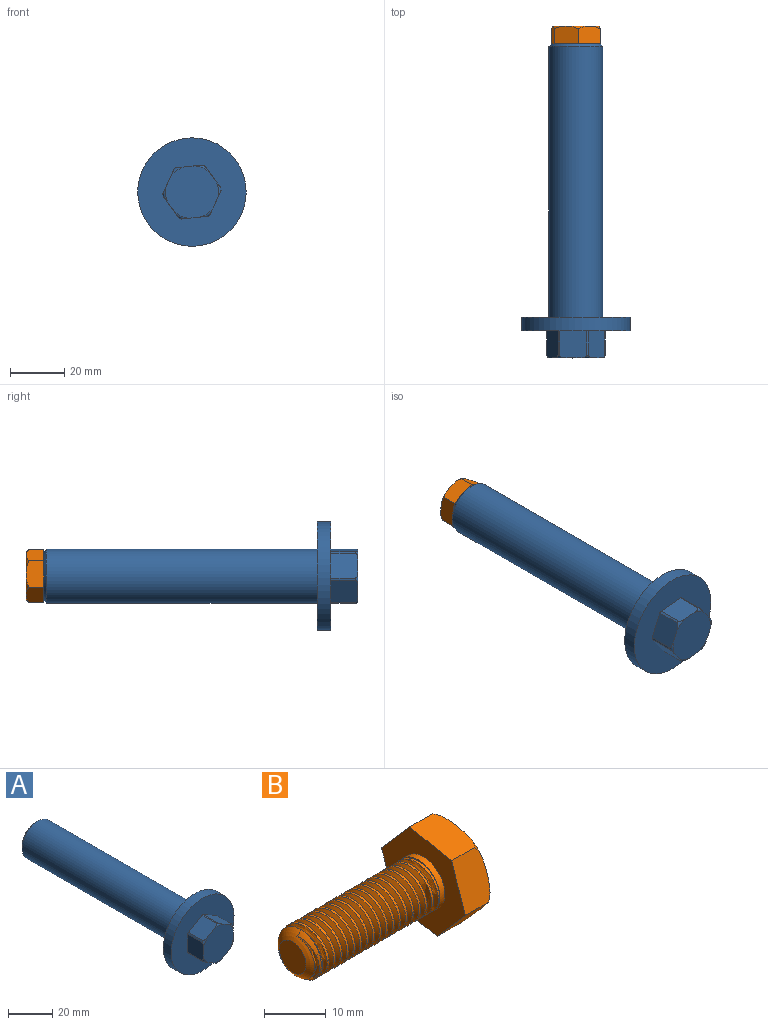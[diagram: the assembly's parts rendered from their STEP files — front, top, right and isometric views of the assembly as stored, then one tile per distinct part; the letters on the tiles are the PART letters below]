
ASSEMBLY  parts=2 mates=1
PART A: 31 faces, bbox 40x116.6x40 mm
  f0: cylinder r=4.25mm len=34.98mm, axis (0,-1,0), area 369.2mm2, adj f2,f3,f15,f29,f30
  f1: plane 17.97x17.97mm, normal (0,1,0), area 174.4mm2, adj f2,f3,f22,f30
  f2: bspline ~35.78x11.94mm, area 726mm2, adj f0,f1,f3,f29,f30
  f3: bspline ~36.03x11.94mm, area 738.2mm2, adj f0,f1,f2,f29,f30
  f4: cylinder r=10.75mm len=9mm, axis (0,-1,0), area 7.1mm2, adj f5,f19,f23,f28
  f5: torus R=9.75mm, axis (0,-1,0), area 3.7mm2, adj f4,f21,f23,f28
  f6: torus R=9.75mm, axis (0,-1,0), area 3.7mm2, adj f12,f21,f24,f28
  f7: cylinder r=10.75mm len=9mm, axis (0,-1,0), area 7.1mm2, adj f8,f19,f24,f27
  f8: torus R=9.75mm, axis (0,-1,0), area 3.7mm2, adj f7,f21,f24,f27
  f9: torus R=9.75mm, axis (0,-1,0), area 3.7mm2, adj f11,f21,f25,f27
  f10: cylinder r=10.75mm len=9mm, axis (0,-1,0), area 7.1mm2, adj f13,f19,f23,f26
  f11: cylinder r=10.75mm len=9mm, axis (0,-1,0), area 7.1mm2, adj f9,f19,f25,f27
  f12: cylinder r=10.75mm len=9mm, axis (0,-1,0), area 7.1mm2, adj f6,f19,f24,f28
  f13: torus R=9.75mm, axis (0,-1,0), area 3.7mm2, adj f10,f21,f23,f26
  f14: torus R=9.75mm, axis (0,-1,0), area 3.7mm2, adj f20,f21,f25,f26
  f15: cone r=4.25mm half-angle=45deg, axis (0,1,0), area 80.2mm2, adj f0
  f16: cylinder r=9.97mm len=100mm, axis (0,-1,0), area 6267.5mm2, adj f17,f22
  f17: plane 40x40mm, normal (0,1,0), area 944mm2, adj f16,f18
  f18: cylinder r=20mm len=40mm, axis (0,-1,0), area 628.3mm2, adj f17,f19
  f19: plane 40x40mm, normal (0,-1,0), area 944.5mm2, adj f4,f7,f10,f11,f12,f18,f20,f23
  f20: cylinder r=10.75mm len=9mm, axis (0,-1,0), area 7.1mm2, adj f14,f19,f25,f26
  f21: plane 19.5x19mm, normal (0,-1,0), area 294.2mm2, adj f5,f6,f8,f9,f13,f14,f23,f24
  f22: cone r=9.97mm half-angle=45deg, axis (0,-1,0), area 84.2mm2, adj f1,f16
  f23: plane 10x8.71mm, normal (0.5,0,0.87), area 99.6mm2, adj f4,f5,f10,f13,f19,f21
  f24: plane 10.06x10mm, normal (-1,0,0), area 99.6mm2, adj f6,f7,f8,f12,f19,f21
  f25: plane 10x8.71mm, normal (0.5,0,-0.87), area 99.6mm2, adj f9,f11,f14,f19,f20,f21
  f26: plane 10.06x10mm, normal (1,0,0), area 99.6mm2, adj f10,f13,f14,f19,f20,f21
  f27: plane 10x8.71mm, normal (-0.5,0,-0.87), area 99.6mm2, adj f7,f8,f9,f11,f19,f21
  f28: plane 10x8.71mm, normal (-0.5,0,0.87), area 99.6mm2, adj f4,f5,f6,f12,f19,f21
  f29: plane 1.06x0.8mm, normal (-0.87,0,-0.5), area 0.5mm2, adj f0,f2,f3
  f30: cone r=5.69mm half-angle=44.1deg, axis (0,1,0), area 18.1mm2, adj f0,f1,f2,f3
PART B: 17 faces, bbox 37.1x20.2x20.2 mm
  f0: plane 7.39x6.5mm, normal (0,0.75,0.66), area 60.9mm2, adj f1,f5,f6,f15
  f1: plane 9.63x6.5mm, normal (0,-0.19,0.98), area 60.9mm2, adj f0,f2,f6,f15
  f2: plane 9.29x6.5mm, normal (0,-0.95,0.32), area 60.9mm2, adj f1,f3,f6,f15
  f3: plane 7.39x6.5mm, normal (0,-0.75,-0.66), area 60.9mm2, adj f2,f4,f6,f15
  f4: plane 9.63x6.5mm, normal (0,0.19,-0.98), area 60.9mm2, adj f3,f5,f6,f15
  f5: plane 9.29x6.5mm, normal (0,0.95,-0.32), area 60.9mm2, adj f0,f4,f6,f15
  f6: plane 19.26x18.58mm, normal (-1,0,0), area 173.3mm2, adj f0,f1,f2,f3,f4,f5,f8
  f7: plane 10.43x10.43mm, normal (-1,0,0), area 11mm2, adj f8,f12,f13,f14
  f8: cylinder r=4.95mm len=9.9mm, axis (1,0,0), area 37.3mm2, adj f6,f7
  f9: plane 6.1x6.1mm, normal (-1,0,0), area 29.2mm2, adj f11
  f10: revolved ~7.92x4.55mm, area 7mm2, adj f11,f12,f13,f14
  f11: revolved ~9.68x9.68mm, area 42.9mm2, adj f9,f10,f13
  f12: bspline ~29.03x11.32mm, area 548mm2, adj f7,f10,f13,f14
  f13: bspline ~29.53x11.32mm, area 544mm2, adj f7,f10,f11,f12,f14
  f14: cylinder r=4.9mm len=27.14mm, axis (-1,0,0), area 221.9mm2, adj f7,f10,f12,f13
  f15: revolved ~19.63x19.63mm, area 36mm2, adj f0,f1,f2,f3,f4,f5,f16
  f16: plane 16.73x16.73mm, normal (1,0,0), area 219.8mm2, adj f15
PLACE A rot(axis=(0,1,0),144deg) t=(9.66,-46.78,9.26)mm
PLACE B rot(axis=(-0.3,-0.3,0.91),95.5deg) t=(9.66,-26.28,9.26)mm
MATE cylindrical B.f8 <-> A.f0  axis (0,-1,0) through (9.66,3.72,9.26)mm
